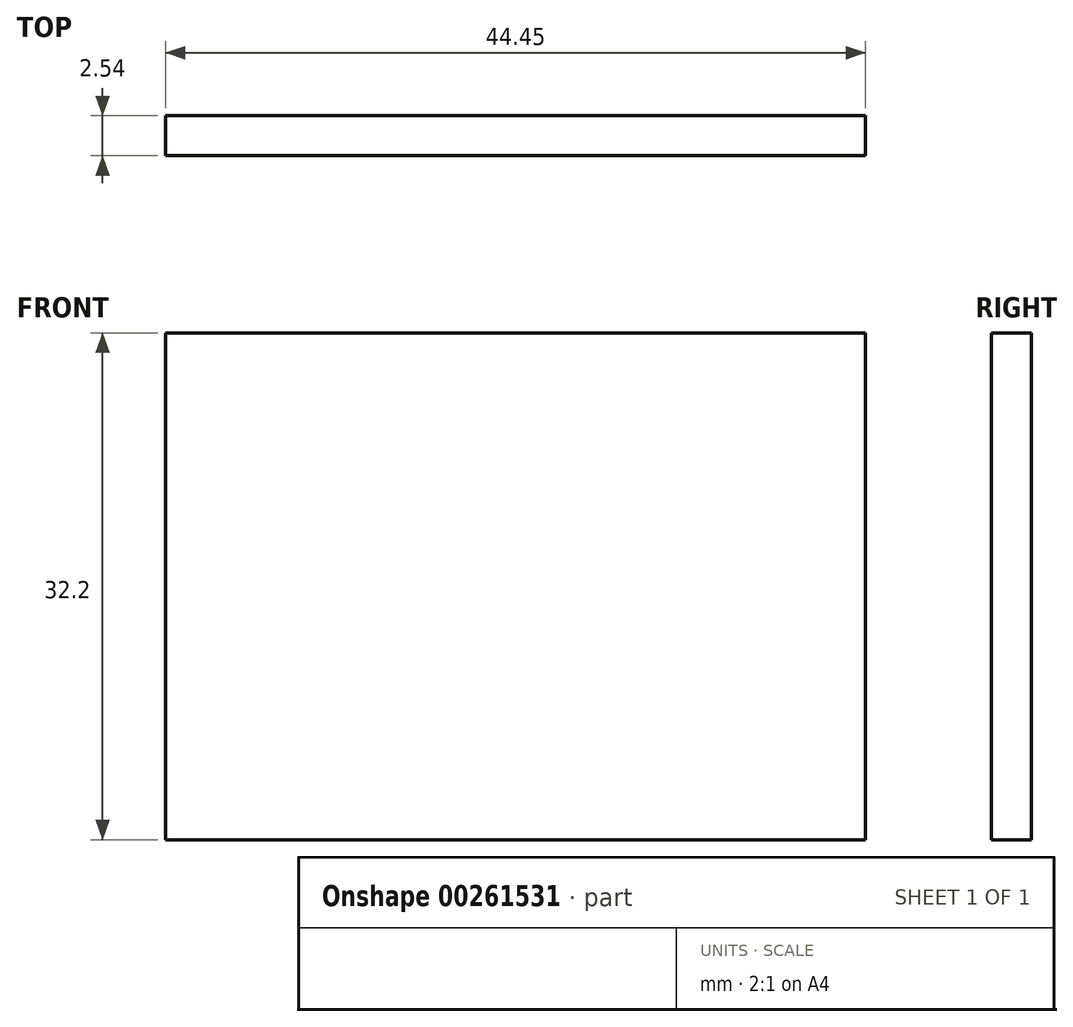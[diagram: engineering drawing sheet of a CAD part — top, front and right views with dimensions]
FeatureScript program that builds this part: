
annotation { "Feature Type Name" : "Feature", "Feature Type Description" : "" }
export const myFeature = defineFeature(function(context is Context, id is Id, definition is map)
    precondition{}
    {
        {
            var Q0;
            Q0=qCreatedBy(makeId("Front.planeOp"),FACE);
            var sketch = newSketch(context, id + "F0", { "sketchPlane" : qUnion([Q0])});
            skLineSegment(sketch, "E0.bottom", {"start": v(0, 0) * mm, "end": v(-44.45, 0) * mm});
            skLineSegment(sketch, "E0.top", {"start": v(0, 32.2) * mm, "end": v(-44.45, 32.2) * mm});
            skLineSegment(sketch, "E0.left", {"start": v(0, 0) * mm, "end": v(0, 32.2) * mm});
            skLineSegment(sketch, "E0.right", {"start": v(-44.45, 0) * mm, "end": v(-44.45, 32.2) * mm});
            skSolve(sketch);
        }
        {
            var Q0;
            Q0=makeQuery(id+"F0.imprint","IMPRINT",FACE,{"disambiguationData":[TD([[makeQuery(id+"F0.imprint","IMPRINT",EDGE,{"derivedFrom":sQuery(id+"F0.wireOp",EDGE,"E0.bottom")}),-1.0]])]});
            extrude(context, id + "F1", {"entities" : qUnion([Q0]), "depth" : 2.54 * mm});
        }
    });
